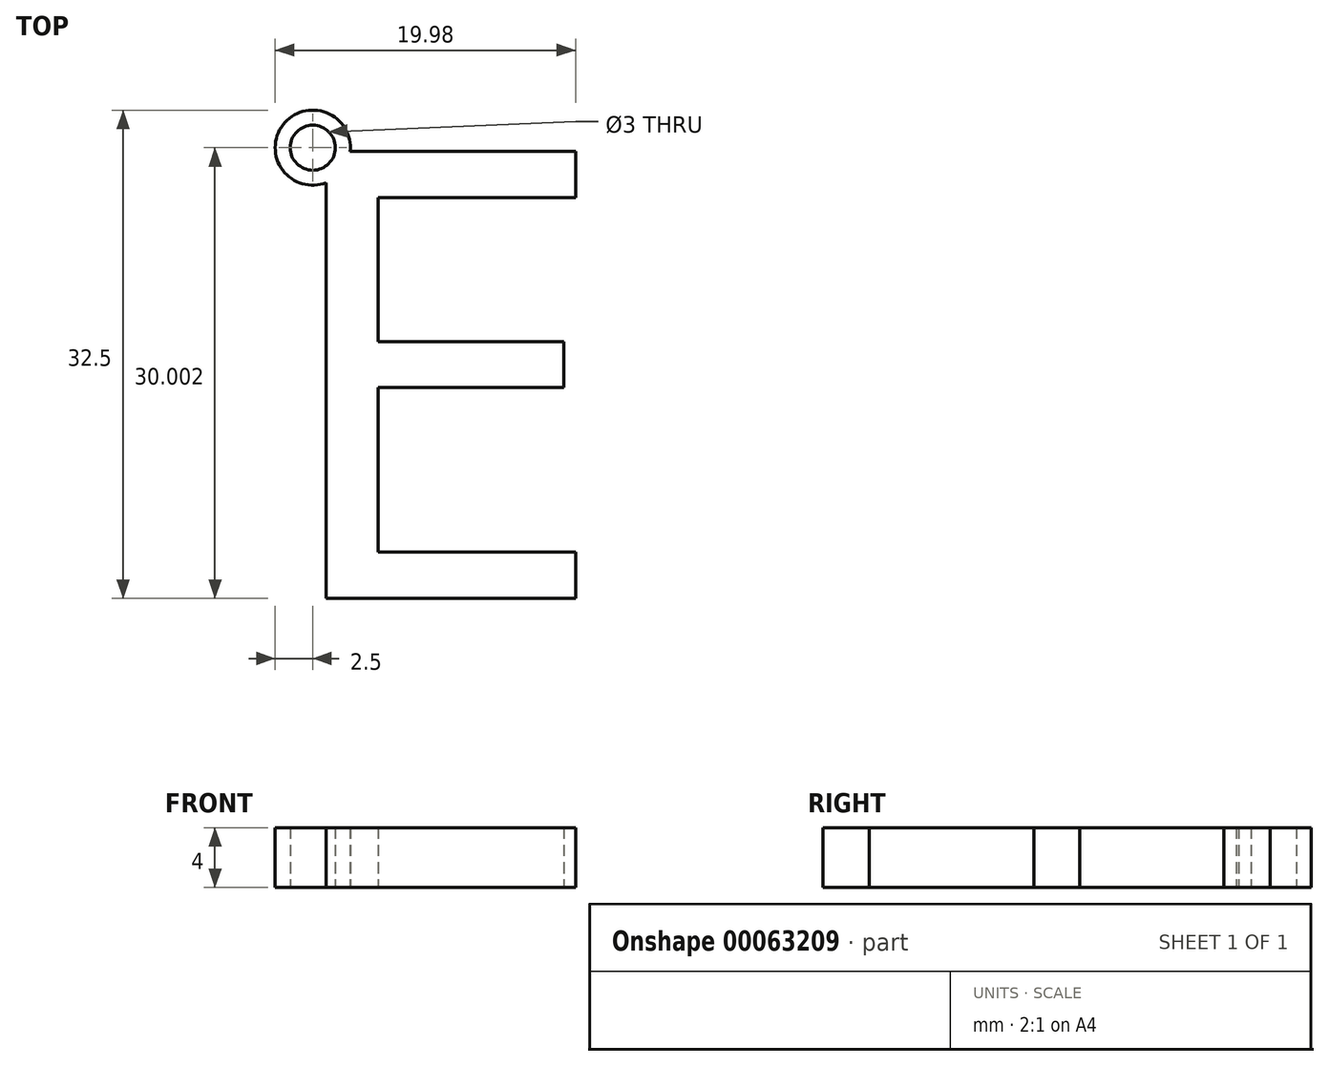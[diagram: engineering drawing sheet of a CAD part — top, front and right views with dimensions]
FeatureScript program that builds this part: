
annotation { "Feature Type Name" : "Feature", "Feature Type Description" : "" }
export const myFeature = defineFeature(function(context is Context, id is Id, definition is map)
    precondition{}
    {
        {
            var Q0;
            Q0=qCreatedBy(makeId("Top.planeOp"),FACE);
            var sketch = newSketch(context, id + "F0", { "sketchPlane" : qUnion([Q0])});
            skText(sketch, "E0", { "text": "E", "fontName": "OpenSans-Regular.ttf"});
            skCircle(sketch, "E1", {"center": v(-22.23, 27.68) * mm, "radius": 1.5 * mm});
            skCircle(sketch, "E2", {"center": v(-22.23, 27.68) * mm, "radius": 2.5 * mm});
            const initialGuessF0  = {"E0": [-0.02542, -0.00232, 1, 0, 0.03]};
            skSetInitialGuess(sketch, initialGuessF0);
            skSolve(sketch);
        }
        {
            var Q0;
            Q0 = qSketchRegion(id + "F0", true);
            extrude(context, id + "F1", {"entities" : qUnion([Q0]), "depth" : 4 * mm});
        }
    });
